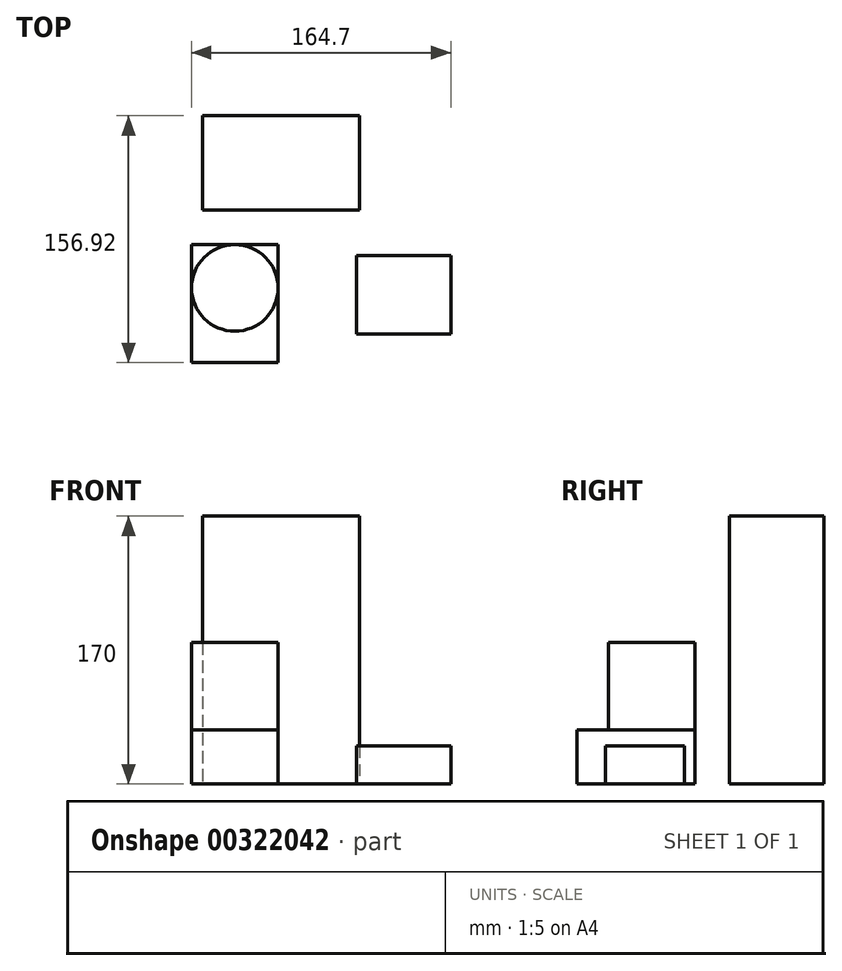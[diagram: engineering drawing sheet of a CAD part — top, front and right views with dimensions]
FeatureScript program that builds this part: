
annotation { "Feature Type Name" : "Feature", "Feature Type Description" : "" }
export const myFeature = defineFeature(function(context is Context, id is Id, definition is map)
    precondition{}
    {
        {
            var Q0;
            Q0=qCreatedBy(makeId("Top.planeOp"),FACE);
            var sketch = newSketch(context, id + "F0", { "sketchPlane" : qUnion([Q0])});
            skLineSegment(sketch, "E0.bottom", {"start": v(-93.31, -5.97) * mm, "end": v(-38.31, -5.97) * mm});
            skLineSegment(sketch, "E0.top", {"start": v(-93.31, -80.97) * mm, "end": v(-38.31, -80.97) * mm});
            skLineSegment(sketch, "E0.left", {"start": v(-93.31, -5.97) * mm, "end": v(-93.31, -80.97) * mm});
            skLineSegment(sketch, "E0.right", {"start": v(-38.31, -5.97) * mm, "end": v(-38.31, -80.97) * mm});
            skCircle(sketch, "E1", {"center": v(-65.81, -33.47) * mm, "radius": 27.5 * mm});
            skLineSegment(sketch, "E2.bottom", {"start": v(11.39, -12.75) * mm, "end": v(71.39, -12.75) * mm});
            skLineSegment(sketch, "E2.top", {"start": v(11.39, -62.75) * mm, "end": v(71.39, -62.75) * mm});
            skLineSegment(sketch, "E2.left", {"start": v(11.39, -12.75) * mm, "end": v(11.39, -62.75) * mm});
            skLineSegment(sketch, "E2.right", {"start": v(71.39, -12.75) * mm, "end": v(71.39, -62.75) * mm});
            skLineSegment(sketch, "E3.bottom", {"start": v(-86.48, 75.95) * mm, "end": v(13.52, 75.95) * mm});
            skLineSegment(sketch, "E3.top", {"start": v(-86.48, 15.95) * mm, "end": v(13.52, 15.95) * mm});
            skLineSegment(sketch, "E3.left", {"start": v(-86.48, 75.95) * mm, "end": v(-86.48, 15.95) * mm});
            skLineSegment(sketch, "E3.right", {"start": v(13.52, 75.95) * mm, "end": v(13.52, 15.95) * mm});
            skSolve(sketch);
        }
        {
            var Q0;
            Q0=makeQuery(id+"F0.imprint","IMPRINT",FACE,{"disambiguationData":[TD([[makeQuery(id+"F0.imprint","IMPRINT",EDGE,{"derivedFrom":sQuery(id+"F0.wireOp",EDGE,"E3.bottom")}),-1.0]])]});
            extrude(context, id + "F1", {"entities" : qUnion([Q0]), "depth" : 170 * mm});
        }
        {
            var Q0;
            {var subQ0=sQuery(id+"F0.wireOp",EDGE,"E1");var subQ1=makeQuery(id+"F0.imprint","INTERSECT",VERTEX,{"derivedFrom":[sQuery(id+"F0.wireOp",EDGE,"E0.bottom"),subQ0]});Q0=makeQuery(id+"F0.imprint","IMPRINT",FACE,{"disambiguationData":[TD([[makeQuery(id+"F0.imprint","IMPRINT",EDGE,{"disambiguationData":[TD([[subQ1,1.0]])],"derivedFrom":subQ0}),1.0]])]});}
            extrude(context, id + "F2", {"entities" : qUnion([Q0]), "depth" : 89.9 * mm});
        }
        {
            var Q0;
            {var subQ0=sQuery(id+"F0.wireOp",EDGE,"E0.top");Q0=makeQuery(id+"F0.imprint","IMPRINT",FACE,{"disambiguationData":[TD([[makeQuery(id+"F0.imprint","IMPRINT",EDGE,{"derivedFrom":subQ0}),1.0]])]});}
            var Q1;
            {var subQ0=sQuery(id+"F0.wireOp",EDGE,"E0.left");var subQ1=sQuery(id+"F0.wireOp",EDGE,"E0.bottom");var subQ2=makeQuery(id+"F0.imprint","INTERSECT",VERTEX,{"derivedFrom":[subQ1,subQ0]});Q1=makeQuery(id+"F0.imprint","IMPRINT",FACE,{"disambiguationData":[TD([[makeQuery(id+"F0.imprint","IMPRINT",EDGE,{"disambiguationData":[TD([[subQ2,-1.0]])],"derivedFrom":subQ1}),-1.0]])]});}
            var Q2;
            {var subQ0=sQuery(id+"F0.wireOp",EDGE,"E0.right");var subQ1=sQuery(id+"F0.wireOp",EDGE,"E0.bottom");var subQ2=makeQuery(id+"F0.imprint","INTERSECT",VERTEX,{"derivedFrom":[subQ1,subQ0]});Q2=makeQuery(id+"F0.imprint","IMPRINT",FACE,{"disambiguationData":[TD([[makeQuery(id+"F0.imprint","IMPRINT",EDGE,{"disambiguationData":[TD([[subQ2,1.0]])],"derivedFrom":subQ1}),-1.0]])]});}
            extrude(context, id + "F3", {"entities" : qUnion([Q0, Q1, Q2]), "operationType" : NewBodyOperationType.ADD, "depth" : 34.4 * mm});
        }
        {
            var Q0;
            Q0=makeQuery(id+"F0.imprint","IMPRINT",FACE,{"disambiguationData":[TD([[makeQuery(id+"F0.imprint","IMPRINT",EDGE,{"derivedFrom":sQuery(id+"F0.wireOp",EDGE,"E2.bottom")}),-1.0]])]});
            extrude(context, id + "F4", {"entities" : qUnion([Q0]), "depth" : 24 * mm});
        }
    });
